FCSTD DOCUMENT  (FreeCAD 0.19R24267 (Git))
Label: single_dot_display_assem
License: All rights reserved
LicenseURL: http://en.wikipedia.org/wiki/All_rights_reserved
objects: App::Link×3, App::DocumentObjectGroup×2, PartDesign::CoordinateSystem×1, App::FeaturePython×1, App::Part×1
note: 1 computed .brp shape members not serialized (recipe doc carries the construction recipe); baked Part::Feature solids carry a one-line shape summary decoded from their .brp
EXTERNAL_REF file=single_dot_dislay_box.FCStd obj=Local_CS
EXTERNAL_REF file=single_dot_dislay_box.FCStd obj=Body
EXTERNAL_REF file=single_dot_display_lid.FCStd obj=Local_CS
EXTERNAL_REF file=single_dot_display_lid.FCStd obj=Body
EXTERNAL_REF file=mom_switch.FCStd obj=Local_CS
EXTERNAL_REF file=single_dot_display_lid.FCStd obj=Local_CS001
EXTERNAL_REF file=mom_switch.FCStd obj=Body

FEATURE [App::DocumentObjectGroup] Parts
FEATURE [PartDesign::CoordinateSystem] LCS_Origin
  AttacherType = Attacher::AttachEngine3D
  MapMode = 2
  Support = -> [X_Axis]
FEATURE [App::DocumentObjectGroup] Constraints
FEATURE [App::FeaturePython] Variables  # WARN: FeaturePython — macro-defined, semantics opaque (R4)
FEATURE [App::Link] single_dot_dislay_box_Body
  AssemblyType = Asm4EE
  AttachedBy = #Local_CS
  AttachedTo = Parent Assembly#LCS_Origin
  LinkPlacement = pos=(55,22.5,-45) rot=(0,0,-1;1.5708rad)
  LinkedObject = -> <external single_dot_dislay_box.FCStd>#Body
  Placement = pos=(55,22.5,-45) rot=(0,0,-1;1.5708rad)
  expr: Placement = LCS_Origin.Placement * AttachmentOffset * single_dot_dislay_box#Local_CS.Placement ^ -1
FEATURE [App::Link] single_dot_display_lid_Body
  AssemblyType = Asm4EE
  AttachedBy = #Local_CS
  AttachedTo = single_dot_dislay_box_Body#Local_CS
  LinkPlacement = pos=(87.5,22.5,0) rot=(0,0,1;1.5708rad)
  LinkedObject = -> <external single_dot_display_lid.FCStd>#Body
  Placement = pos=(87.5,22.5,0) rot=(0,0,1;1.5708rad)
  expr: Placement = single_dot_dislay_box_Body.Placement * single_dot_dislay_box#Local_CS.Placement * AttachmentOffset * single_dot_display_lid#Local_CS.Placement ^ -1
FEATURE [App::Link] Unnamed1_Body
  AssemblyType = Asm4EE
  AttachedBy = #Local_CS
  AttachedTo = single_dot_display_lid_Body#Local_CS001
  LinkPlacement = pos=(27.5,22.5,-32) rot=(0,0,1;4.71239rad)
  LinkedObject = -> <external mom_switch.FCStd>#Body
  Placement = pos=(27.5,22.5,-32) rot=(0,0,1;4.71239rad)
  expr: Placement = single_dot_display_lid_Body.Placement * single_dot_display_lid#Local_CS001.Placement * AttachmentOffset * mom_switch#Local_CS.Placement ^ -1
FEATURE [App::Part] Model
  Configuration = 0
  Group = -> [LCS_Origin,Constraints,Variables,single_dot_dislay_box_Body,single_dot_display_lid_Body,Unnamed1_Body]
  Origin = -> Origin
  Type = Assembly4 Model

RESOLVED EXTERNAL PARTS (link-assembly join: the EXTERNAL_REF files above that resolve inside this repo's crawl, each included once):
---- part mom_switch.FCStd = doc fcstd_50052116598c ----
FCSTD DOCUMENT  (FreeCAD 0.19R24267 (Git))
Label: mom_switch
License: All rights reserved
LicenseURL: http://en.wikipedia.org/wiki/All_rights_reserved
objects: Sketcher::SketchObject×5, PartDesign::Pad×4, PartDesign::Pocket×1, PartDesign::Mirrored×1, PartDesign::Chamfer×1, PartDesign::CoordinateSystem×1, PartDesign::Body×1
note: 20 computed .brp shape members not serialized (recipe doc carries the construction recipe); baked Part::Feature solids carry a one-line shape summary decoded from their .brp

FEATURE [Sketcher::SketchObject] Sketch
  FullyConstrained = true
  MapMode = 5
  Support = -> [XY_Plane]
  sketch-geometry (4):
    g0: LineSegment StartX=-16.5 StartY=9.5 StartZ=0 EndX=16.5 EndY=9.5 EndZ=0
    g1: LineSegment StartX=16.5 StartY=9.5 StartZ=0 EndX=16.5 EndY=-9.5 EndZ=0
    g2: LineSegment StartX=16.5 StartY=-9.5 StartZ=0 EndX=-16.5 EndY=-9.5 EndZ=0
    g3: LineSegment StartX=-16.5 StartY=-9.5 StartZ=0 EndX=-16.5 EndY=9.5 EndZ=0
  constraints (12):
    c: Coincident(g0,g1)
    c: Coincident(g1,g2)
    c: Coincident(g2,g3)
    c: Coincident(g3,g0)
    c: Horizontal(g0)
    c: Horizontal(g2)
    c: Vertical(g1)
    c: Vertical(g3)
    c: Distance(g0) = 33
    c: Distance(g3) = 19
    c: DistanceX(g0) = 16.5
    c: DistanceY(g0) = 9.5
FEATURE [PartDesign::Pad] Pad
  Direction = (1,1,1)
  Length = 25
  Length2 = 100
  Profile = -> Sketch
  Refine = true
  Type = 0
FEATURE [Sketcher::SketchObject] Sketch001
  FullyConstrained = true
  MapMode = 5
  Placement = pos=(0,0,25) rot=(0,0,1;0rad)
  Support = -> [Pad]
  sketch-geometry (1):
    g0: Circle CenterX=0 CenterY=0 CenterZ=0 NormalX=0 NormalY=0 NormalZ=1 AngleXU=0 Radius=6
  constraints (2):
    c: Coincident(g0,g-1)
    c: Radius(g0) = 6
FEATURE [PartDesign::Pad] Pad001
  BaseFeature = -> Pad
  Direction = (1,1,1)
  Length = 12
  Length2 = 100
  Profile = -> Sketch001
  Refine = true
  Type = 0
FEATURE [Sketcher::SketchObject] Sketch002
  FullyConstrained = true
  MapMode = 5
  Placement = pos=(0,0,37) rot=(0,0,1;0rad)
  Support = -> [Pad001]
  sketch-geometry (1):
    g0: Circle CenterX=0 CenterY=0 CenterZ=0 NormalX=0 NormalY=0 NormalZ=1 AngleXU=0 Radius=2
  constraints (2):
    c: Coincident(g0,g-1)
    c: Radius(g0) = 2
FEATURE [PartDesign::Pad] Pad002
  BaseFeature = -> Pad001
  Direction = (1,1,1)
  Length = 3.6
  Length2 = 100
  Profile = -> Sketch002
  Refine = true
  Type = 0
FEATURE [Sketcher::SketchObject] Sketch003
  FullyConstrained = true
  MapMode = 5
  Placement = pos=(0,0,40.6) rot=(0,0,1;0rad)
  Support = -> [Pad002]
  sketch-geometry (5):
    g0: LineSegment StartX=4.5 StartY=-4.5 StartZ=0 EndX=4.5 EndY=4.5 EndZ=0
    g1: LineSegment StartX=4.5 StartY=4.5 StartZ=0 EndX=-4.5 EndY=4.5 EndZ=0
    g2: LineSegment StartX=-4.5 StartY=4.5 StartZ=0 EndX=-4.5 EndY=-4.5 EndZ=0
    g3: LineSegment StartX=-4.5 StartY=-4.5 StartZ=0 EndX=4.5 EndY=-4.5 EndZ=0
    g4: Circle CenterX=0 CenterY=0 CenterZ=0 NormalX=0 NormalY=0 NormalZ=1 AngleXU=0 Radius=6.36396
  constraints (14):
    c: Coincident(g0,g1)
    c: Coincident(g1,g2)
    c: Coincident(g2,g3)
    c: Coincident(g3,g0)
    c: Equal(g0,g1)
    c: Equal(g0,g2)
    c: Equal(g0,g3)
    c: PointOnObject(g0,g4)
    c: PointOnObject(g1,g4)
    c: PointOnObject(g2,g4)
    c: PointOnObject(g3,g4)
    c: Coincident(g4,g-1)
    c: Horizontal(g1)
    c: Distance(g1) = 9
FEATURE [PartDesign::Pad] Pad003
  BaseFeature = -> Pad002
  Direction = (1,1,1)
  Length = 23
  Length2 = 100
  Profile = -> Sketch003
  Refine = true
  Type = 0
FEATURE [Sketcher::SketchObject] Sketch004
  ExternalGeometry = -> [Pad003]
  FullyConstrained = false
  MapMode = 5
  Placement = pos=(4e-16,-4.5,0) rot=(1,0,0;1.5708rad)
  Support = -> [Pad003]
  sketch-geometry (3):
    g0: LineSegment StartX=-4.5 StartY=40.6 StartZ=0 EndX=-2.21452 EndY=63.6 EndZ=0
    g1: LineSegment StartX=-2.21452 StartY=63.6 StartZ=0 EndX=-4.5 EndY=63.6 EndZ=0
    g2: LineSegment StartX=-4.5 StartY=40.6 StartZ=0 EndX=-4.5 EndY=63.6 EndZ=0
  constraints (6):
    c: Coincident(g0,g-4)
    c: PointOnObject(g0,g-5)
    c: Coincident(g1,g0)
    c: Coincident(g1,g-5)
    c: Coincident(g2,g0)
    c: Coincident(g2,g1)
FEATURE [PartDesign::Pocket] Pocket
  BaseFeature = -> Pad003
  Length = 13
  Length2 = 100
  Profile = -> Sketch004
  Refine = true
  Type = 0
FEATURE [PartDesign::Mirrored] Mirrored
  BaseFeature = -> Pocket
  MirrorPlane = -> Sketch004 [V_Axis]
  Originals = -> [Pocket]
  Refine = true
FEATURE [PartDesign::Chamfer] Chamfer
  Angle = 45
  Base = -> Mirrored [Edge10,Edge2,Edge6,Edge4,Edge11,Edge8,Edge3,Edge7,Edge9,Edge13,Edge12,Edge1]
  BaseFeature = -> Mirrored
  ChamferType = 0
  FlipDirection = false
  Refine = true
  Size = 1
  Size2 = 1
  SupportTransform = false
FEATURE [PartDesign::CoordinateSystem] Local_CS  label="switch_center"
  AttacherType = Attacher::AttachEngine3D
  MapMode = 5
  Placement = pos=(0,0,37) rot=(0,0,1;0rad)
  Support = -> [Chamfer]
FEATURE [PartDesign::Body] Body
  Group = -> [Sketch,Pad,Sketch001,Pad001,Sketch002,Pad002,Sketch003,Pad003,Sketch004,Pocket,Mirrored,Chamfer,Local_CS]
  Origin = -> Origin
  Tip = -> Chamfer
---- part single_dot_dislay_box.FCStd = doc fcstd_fc865e79ae6e ----
FCSTD DOCUMENT  (FreeCAD 0.19R24267 (Git))
Label: single_dot_dislay_box
License: All rights reserved
LicenseURL: http://en.wikipedia.org/wiki/All_rights_reserved
objects: Sketcher::SketchObject×5, PartDesign::Pad×3, PartDesign::Pocket×2, PartDesign::CoordinateSystem×1, PartDesign::Body×1
note: 17 computed .brp shape members not serialized (recipe doc carries the construction recipe); baked Part::Feature solids carry a one-line shape summary decoded from their .brp

FEATURE [Sketcher::SketchObject] Sketch
  FullyConstrained = true
  MapMode = 5
  Support = -> [XY_Plane]
  sketch-geometry (4):
    g0: LineSegment StartX=-30 StartY=62.5 StartZ=0 EndX=30 EndY=62.5 EndZ=0
    g1: LineSegment StartX=30 StartY=62.5 StartZ=0 EndX=30 EndY=-62.5 EndZ=0
    g2: LineSegment StartX=30 StartY=-62.5 StartZ=0 EndX=-30 EndY=-62.5 EndZ=0
    g3: LineSegment StartX=-30 StartY=-62.5 StartZ=0 EndX=-30 EndY=62.5 EndZ=0
  constraints (12):
    c: Coincident(g0,g1)
    c: Coincident(g1,g2)
    c: Coincident(g2,g3)
    c: Coincident(g3,g0)
    c: Horizontal(g0)
    c: Horizontal(g2)
    c: Vertical(g1)
    c: Vertical(g3)
    c: Distance(g0) = 60
    c: Distance(g3) = 125
    c: DistanceX(g-2,g0) = 30
    c: DistanceY(g-1,g0) = 62.5
FEATURE [PartDesign::Pad] Pad
  Direction = (1,1,1)
  Length = 45
  Length2 = 100
  Profile = -> Sketch
  Refine = true
  Type = 0
FEATURE [Sketcher::SketchObject] Sketch001
  ExternalGeometry = -> [Pad]
  FullyConstrained = true
  MapMode = 5
  Placement = pos=(0,0,45) rot=(0,0,1;0rad)
  Support = -> [Pad]
  sketch-geometry (4):
    g0: LineSegment StartX=-27 StartY=59.5 StartZ=0 EndX=27 EndY=59.5 EndZ=0
    g1: LineSegment StartX=27 StartY=59.5 StartZ=0 EndX=27 EndY=-59.5 EndZ=0
    g2: LineSegment StartX=27 StartY=-59.5 StartZ=0 EndX=-27 EndY=-59.5 EndZ=0
    g3: LineSegment StartX=-27 StartY=-59.5 StartZ=0 EndX=-27 EndY=59.5 EndZ=0
  constraints (12):
    c: Coincident(g0,g1)
    c: Coincident(g1,g2)
    c: Coincident(g2,g3)
    c: Coincident(g3,g0)
    c: Horizontal(g0)
    c: Horizontal(g2)
    c: Vertical(g1)
    c: Vertical(g3)
    c: DistanceX(g0,g-5) = -3
    c: DistanceY(g0,g-5) = 3
    c: DistanceX(g1,g-4) = 3
    c: DistanceY(g1,g-4) = -3
FEATURE [PartDesign::Pocket] Pocket
  BaseFeature = -> Pad
  Length = 42
  Length2 = 100
  Profile = -> Sketch001
  Refine = true
  Type = 0
FEATURE [Sketcher::SketchObject] Sketch002
  ExternalGeometry = -> [Pocket]
  FullyConstrained = false
  MapMode = 5
  Placement = pos=(0,0,45) rot=(0,0,1;0rad)
  Support = -> [Pocket]
  sketch-geometry (23):
    g0: LineSegment StartX=30 StartY=-62.5 StartZ=0 EndX=30 EndY=-55 EndZ=0
    g1: LineSegment StartX=30 StartY=-55 StartZ=0 EndX=22.5 EndY=-55 EndZ=0
    g2: Circle CenterX=22.5 CenterY=-55 CenterZ=0 NormalX=0 NormalY=0 NormalZ=1 AngleXU=0 Radius=2.25
    g3: ArcOfCircle CenterX=22.5 CenterY=-55 CenterZ=0 NormalX=0 NormalY=0 NormalZ=1 AngleXU=0 Radius=3.75 StartAngle=1.5708 EndAngle=3.14159
    g4: LineSegment StartX=18.75 StartY=-60.4455 StartZ=0 EndX=18.75 EndY=-55 EndZ=0
    g5: LineSegment StartX=27.7509 StartY=-51.25 StartZ=0 EndX=22.5 EndY=-51.25 EndZ=0
    g6: LineSegment StartX=27.7509 StartY=-51.25 StartZ=0 EndX=27 EndY=-59.5 EndZ=0
    g7: LineSegment StartX=18.75 StartY=-60.4455 StartZ=0 EndX=27 EndY=-59.5 EndZ=0
    g8: LineSegment StartX=-18.75 StartY=-60.4455 StartZ=0 EndX=-27 EndY=-59.5 EndZ=0
    g9: LineSegment StartX=-18.75 StartY=-60.4455 StartZ=0 EndX=-18.75 EndY=-55 EndZ=0
    g10: ArcOfCircle CenterX=-22.5 CenterY=-55 CenterZ=0 NormalX=0 NormalY=0 NormalZ=1 AngleXU=0 Radius=3.75 StartAngle=0 EndAngle=1.5708
    g11: LineSegment StartX=-27.7509 StartY=-51.25 StartZ=0 EndX=-22.5 EndY=-51.25 EndZ=0
    g12: LineSegment StartX=-27.7509 StartY=-51.25 StartZ=0 EndX=-27 EndY=-59.5 EndZ=0
    g13: LineSegment StartX=-18.75 StartY=60.4455 StartZ=0 EndX=-27 EndY=59.5 EndZ=0
    g14: LineSegment StartX=-27.7509 StartY=51.25 StartZ=0 EndX=-27 EndY=59.5 EndZ=0
    g15: LineSegment StartX=-27.7509 StartY=51.25 StartZ=0 EndX=-22.5 EndY=51.25 EndZ=0
    g16: ArcOfCircle CenterX=-22.5 CenterY=55 CenterZ=0 NormalX=0 NormalY=0 NormalZ=1 AngleXU=0 Radius=3.75 StartAngle=4.71239 EndAngle=6.28319
    g17: LineSegment StartX=-18.75 StartY=60.4455 StartZ=0 EndX=-18.75 EndY=55 EndZ=0
    g18: LineSegment StartX=18.75 StartY=60.4455 StartZ=0 EndX=18.75 EndY=55 EndZ=0
    g19: LineSegment StartX=18.75 StartY=60.4455 StartZ=0 EndX=27 EndY=59.5 EndZ=0
    g20: ArcOfCircle CenterX=22.5 CenterY=55 CenterZ=0 NormalX=0 NormalY=0 NormalZ=1 AngleXU=0 Radius=3.75 StartAngle=3.14159 EndAngle=4.71239
    g21: LineSegment StartX=27.7509 StartY=51.25 StartZ=0 EndX=22.5 EndY=51.25 EndZ=0
    g22: LineSegment StartX=27.7509 StartY=51.25 StartZ=0 EndX=27 EndY=59.5 EndZ=0
  constraints (42):
    c: Coincident(g0,g-4)
    c: PointOnObject(g0,g-4)
    c: Coincident(g1,g0)
    c: Horizontal(g1)
    c: Distance(g1) = 7.5
    c: Equal(g0,g1)
    c: Coincident(g2,g1)
    c: Radius(g2) = 2.25
    c: Coincident(g3,g1)
    c: Radius(g3) = 3.75
    c: Vertical(g4)
    c: Horizontal(g5)
    c: Tangent(g3,g4) = 1.5708
    c: Tangent(g3,g5) = -1.5708
    c: Coincident(g6,g5)
    c: Coincident(g6,g-6)
    c: Coincident(g7,g4)
    c: Coincident(g7,g6)
    c: Radius(g10) = 3.75
    c: Vertical(g9)
    c: Horizontal(g11)
    c: Tangent(g10,g9) = -1.5708
    c: Tangent(g10,g11) = 1.5708
    c: Coincident(g12,g11)
    c: Coincident(g8,g9)
    c: Coincident(g8,g12)
    c: Radius(g20) = 3.75
    c: Vertical(g18)
    c: Horizontal(g21)
    c: Tangent(g20,g18) = -1.5708
    c: Tangent(g20,g21) = 1.5708
    c: Coincident(g22,g21)
    c: Coincident(g19,g18)
    c: Coincident(g19,g22)
    c: Radius(g16) = 3.75
    c: Vertical(g17)
    c: Horizontal(g15)
    c: Tangent(g16,g17) = 1.5708
    c: Tangent(g16,g15) = -1.5708
    c: Coincident(g14,g15)
    c: Coincident(g13,g17)
    c: Coincident(g13,g14)
FEATURE [PartDesign::Pad] Pad001
  BaseFeature = -> Pocket
  Direction = (1,1,1)
  Length = 8
  Length2 = 100
  Profile = -> Sketch002
  Refine = true
  Reversed = true
  Type = 0
FEATURE [Sketcher::SketchObject] Sketch003
  ExternalGeometry = -> [Pad001]
  FullyConstrained = false
  MapMode = 5
  Placement = pos=(0,0,45) rot=(0,0,1;0rad)
  Support = -> [Pad001]
  sketch-geometry (4):
    g0: Circle CenterX=22.5 CenterY=55 CenterZ=0 NormalX=0 NormalY=0 NormalZ=1 AngleXU=0 Radius=2.25
    g1: Circle CenterX=-22.5 CenterY=55 CenterZ=0 NormalX=0 NormalY=0 NormalZ=1 AngleXU=0 Radius=2.25
    g2: Circle CenterX=22.5 CenterY=-55 CenterZ=0 NormalX=0 NormalY=0 NormalZ=1 AngleXU=0 Radius=2.25
    g3: Circle CenterX=-22.5 CenterY=-55 CenterZ=0 NormalX=0 NormalY=0 NormalZ=1 AngleXU=0 Radius=2.25
  constraints (5):
    c: Coincident(g0,g-3)
    c: Radius(g0) = 2.25
    c: Radius(g1) = 2.25
    c: Radius(g2) = 2.25
    c: Radius(g3) = 2.25
FEATURE [PartDesign::Pocket] Pocket001
  BaseFeature = -> Pad001
  Length = 7
  Length2 = 100
  Profile = -> Sketch003
  Refine = true
  Type = 0
FEATURE [PartDesign::CoordinateSystem] Local_CS  label="fastener"
  AttacherType = Attacher::AttachEngine3D
  MapMode = 11
  Placement = pos=(22.5,-55,45) rot=(0,0,1;1.5708rad)
  Support = -> [Pocket001]
FEATURE [Sketcher::SketchObject] Sketch004
  FullyConstrained = false
  MapMode = 5
  Placement = pos=(0,0,3) rot=(0,0,1;0rad)
  Support = -> [Pocket001]
  sketch-geometry (34):
    g0: LineSegment StartX=-20 StartY=8 StartZ=0 EndX=24 EndY=8 EndZ=0
    g1: LineSegment StartX=24 StartY=8 StartZ=0 EndX=24 EndY=-8 EndZ=0
    g2: LineSegment StartX=24 StartY=-8 StartZ=0 EndX=-20 EndY=-8 EndZ=0
    g3: LineSegment StartX=-20 StartY=-8 StartZ=0 EndX=-20 EndY=8 EndZ=0
    g4: LineSegment StartX=-18 StartY=8 StartZ=0 EndX=-18 EndY=10 EndZ=0
    g5: LineSegment StartX=-18 StartY=10 StartZ=0 EndX=-22 EndY=10 EndZ=0
    g6: LineSegment StartX=-22 StartY=10 StartZ=0 EndX=-22 EndY=6 EndZ=0
    g7: LineSegment StartX=-22 StartY=6 StartZ=0 EndX=-20 EndY=6 EndZ=0
    g8: Circle CenterX=-20 CenterY=8 CenterZ=0 NormalX=0 NormalY=0 NormalZ=1 AngleXU=0 Radius=2.82843
    g9: LineSegment StartX=-20 StartY=6 StartZ=0 EndX=-20 EndY=8 EndZ=0
    g10: LineSegment StartX=-18 StartY=8 StartZ=0 EndX=-20 EndY=8 EndZ=0
    g11: LineSegment StartX=-18 StartY=-8 StartZ=0 EndX=-18 EndY=-10 EndZ=0
    g12: LineSegment StartX=-18 StartY=-10 StartZ=0 EndX=-22 EndY=-10 EndZ=0
    g13: LineSegment StartX=-22 StartY=-10 StartZ=0 EndX=-22 EndY=-6 EndZ=0
    g14: LineSegment StartX=-22 StartY=-6 StartZ=0 EndX=-20 EndY=-6 EndZ=0
    g15: Circle CenterX=-20 CenterY=-8 CenterZ=0 NormalX=0 NormalY=0 NormalZ=1 AngleXU=0 Radius=2.82843
    g16: LineSegment StartX=-20 StartY=-6 StartZ=0 EndX=-20 EndY=-8 EndZ=0
    g17: LineSegment StartX=-18 StartY=-8 StartZ=0 EndX=-20 EndY=-8 EndZ=0
    g18: LineSegment StartX=0 StartY=0 StartZ=0 EndX=2 EndY=0 EndZ=0
    g19: LineSegment StartX=2 StartY=0 StartZ=0 EndX=2 EndY=-2.88853 EndZ=0
    g20: LineSegment StartX=22 StartY=8 StartZ=0 EndX=22 EndY=10 EndZ=0
    g21: LineSegment StartX=22 StartY=10 StartZ=0 EndX=26 EndY=10 EndZ=0
    g22: LineSegment StartX=26 StartY=10 StartZ=0 EndX=26 EndY=6 EndZ=0
    g23: LineSegment StartX=26 StartY=6 StartZ=0 EndX=24 EndY=6 EndZ=0
    g24: Circle CenterX=24 CenterY=8 CenterZ=0 NormalX=0 NormalY=0 NormalZ=1 AngleXU=0 Radius=2.82843
    g25: LineSegment StartX=24 StartY=6 StartZ=0 EndX=24 EndY=8 EndZ=0
    g26: LineSegment StartX=22 StartY=8 StartZ=0 EndX=24 EndY=8 EndZ=0
    g27: LineSegment StartX=22 StartY=-8 StartZ=0 EndX=22 EndY=-10 EndZ=0
    g28: LineSegment StartX=22 StartY=-10 StartZ=0 EndX=26 EndY=-10 EndZ=0
    g29: LineSegment StartX=26 StartY=-10 StartZ=0 EndX=26 EndY=-6 EndZ=0
    g30: LineSegment StartX=26 StartY=-6 StartZ=0 EndX=24 EndY=-6 EndZ=0
    g31: Circle CenterX=24 CenterY=-8 CenterZ=0 NormalX=0 NormalY=0 NormalZ=1 AngleXU=0 Radius=2.82843
    g32: LineSegment StartX=24 StartY=-6 StartZ=0 EndX=24 EndY=-8 EndZ=0
    g33: LineSegment StartX=22 StartY=-8 StartZ=0 EndX=24 EndY=-8 EndZ=0
  constraints (61):
    c: Coincident(g0,g1)
    c: Coincident(g1,g2)
    c: Coincident(g2,g3)
    c: Coincident(g3,g0)
    c: Horizontal(g0)
    c: Horizontal(g2)
    c: Vertical(g1)
    c: Vertical(g3)
    c: Distance(g0) = 44
    c: Distance(g3) = 16
    c: DistanceX(g0) = 24
    c: DistanceY(g0) = 8
    c: Coincident(g4,g5)
    c: Coincident(g5,g6)
    c: Coincident(g6,g7)
    c: PointOnObject(g4,g8)
    c: PointOnObject(g5,g8)
    c: PointOnObject(g6,g8)
    c: Coincident(g8,g0)
    c: Horizontal(g7)
    c: PointOnObject(g4,g0)
    c: PointOnObject(g7,g3)
    c: Coincident(g9,g7)
    c: Coincident(g9,g0)
    c: Coincident(g10,g4)
    c: Coincident(g10,g9)
    c: Coincident(g11,g12)
    c: Coincident(g12,g13)
    c: Coincident(g13,g14)
    c: PointOnObject(g11,g15)
    c: PointOnObject(g12,g15)
    c: PointOnObject(g13,g15)
    c: Horizontal(g14)
    c: Coincident(g16,g14)
    c: Coincident(g17,g11)
    c: Coincident(g17,g16)
    c: Coincident(g18,g-1)
    c: PointOnObject(g18,g-1)
    c: Distance(g18) = 2
    c: Coincident(g19,g18)
    c: Vertical(g19)
    c: Coincident(g20,g21)
    c: Coincident(g21,g22)
    c: Coincident(g22,g23)
    c: PointOnObject(g20,g24)
    c: PointOnObject(g21,g24)
    c: PointOnObject(g22,g24)
    c: Horizontal(g23)
    c: Coincident(g25,g23)
    c: Coincident(g26,g20)
    c: Coincident(g26,g25)
    c: Coincident(g27,g28)
    c: Coincident(g28,g29)
    c: Coincident(g29,g30)
    c: PointOnObject(g27,g31)
    c: PointOnObject(g28,g31)
    c: PointOnObject(g29,g31)
    c: Horizontal(g30)
    c: Coincident(g32,g30)
    c: Coincident(g33,g27)
    c: Coincident(g33,g32)
FEATURE [PartDesign::Pad] Pad002
  BaseFeature = -> Pocket001
  Direction = (1,1,1)
  Length = 11
  Length2 = 100
  Profile = -> Sketch004
  Refine = true
  Type = 0
FEATURE [PartDesign::Body] Body
  Group = -> [Sketch,Pad,Sketch001,Pocket,Sketch002,Pad001,Sketch003,Pocket001,Local_CS,Sketch004,Pad002]
  Origin = -> Origin
  Tip = -> Pad002
---- part single_dot_display_lid.FCStd = doc fcstd_47c3f7db298e ----
FCSTD DOCUMENT  (FreeCAD 0.19R24267 (Git))
Label: single_dot_display_lid
License: All rights reserved
LicenseURL: http://en.wikipedia.org/wiki/All_rights_reserved
objects: Sketcher::SketchObject×10, PartDesign::Pocket×7, PartDesign::Pad×3, PartDesign::Mirrored×2, PartDesign::Chamfer×2, PartDesign::Point×2, PartDesign::CoordinateSystem×2, PartDesign::Line×1, PartDesign::Body×1
note: 42 computed .brp shape members not serialized (recipe doc carries the construction recipe); baked Part::Feature solids carry a one-line shape summary decoded from their .brp

FEATURE [Sketcher::SketchObject] Sketch
  FullyConstrained = false
  MapMode = 5
  Support = -> [XY_Plane]
  sketch-geometry (7):
    g0: LineSegment StartX=0 StartY=0 StartZ=0 EndX=0 EndY=17.9605 EndZ=0
    g1: LineSegment StartX=0 StartY=0 StartZ=0 EndX=0 EndY=-17.9605 EndZ=0
    g2: LineSegment StartX=0 StartY=-17.9605 StartZ=0 EndX=17.9605 EndY=-1.3181e-12 EndZ=0
    g3: LineSegment StartX=17.9605 StartY=-1.3198e-12 StartZ=0 EndX=7.8018e-12 EndY=17.9605 EndZ=0
    g4: LineSegment StartX=7.8006e-12 StartY=17.9605 StartZ=0 EndX=-17.9605 EndY=5.5387e-12 EndZ=0
    g5: LineSegment StartX=-17.9605 StartY=5.5387e-12 StartZ=0 EndX=0 EndY=-17.9605 EndZ=0
    g6: Circle CenterX=0 CenterY=0 CenterZ=0 NormalX=0 NormalY=0 NormalZ=1 AngleXU=0 Radius=17.9605
  constraints (19):
    c: Coincident(g0,g-1)
    c: Vertical(g0)
    c: Vertical(g1)
    c: Coincident(g2,g3)
    c: Coincident(g3,g4)
    c: Coincident(g4,g5)
    c: Coincident(g5,g2)
    c: Equal(g2,g3)
    c: Equal(g2,g4)
    c: Equal(g2,g5)
    c: PointOnObject(g2,g6)
    c: PointOnObject(g3,g6)
    c: PointOnObject(g4,g6)
    c: PointOnObject(g5,g6)
    c: Coincident(g6,g-1)
    c: Coincident(g5,g1)
    c: Coincident(g1,g-1)
    c: Equal(g1,g0)
    c: Distance(g4) = 25.4
FEATURE [PartDesign::Pad] Pad
  AllowMultiFace = false
  Direction = (1,1,1)
  Length = 22
  Length2 = 100
  Profile = -> Sketch
  Type = 0
FEATURE [Sketcher::SketchObject] Sketch001
  FullyConstrained = false
  MapMode = 5
  Placement = pos=(0,0,22) rot=(0,0,1;0rad)
  Support = -> [Pad]
  sketch-geometry (6):
    g0: LineSegment StartX=0 StartY=14.8492 StartZ=0 EndX=-14.8492 EndY=-1.8e-15 EndZ=0
    g1: LineSegment StartX=-14.8492 StartY=-1.8e-15 StartZ=0 EndX=0 EndY=-14.8492 EndZ=0
    g2: LineSegment StartX=8e-16 StartY=-14.8492 StartZ=0 EndX=14.8492 EndY=0 EndZ=0
    g3: LineSegment StartX=14.8492 StartY=0 StartZ=0 EndX=0 EndY=14.8492 EndZ=0
    g4: Circle CenterX=0 CenterY=0 CenterZ=0 NormalX=0 NormalY=0 NormalZ=1 AngleXU=0 Radius=14.8492
    g5: LineSegment StartX=0 StartY=0 StartZ=0 EndX=0 EndY=14.8492 EndZ=0
  constraints (16):
    c: Coincident(g0,g1)
    c: Coincident(g1,g2)
    c: Coincident(g2,g3)
    c: Coincident(g3,g0)
    c: Equal(g0,g1)
    c: Equal(g0,g2)
    c: Equal(g0,g3)
    c: PointOnObject(g0,g4)
    c: PointOnObject(g1,g4)
    c: PointOnObject(g2,g4)
    c: PointOnObject(g3,g4)
    c: Coincident(g4,g-1)
    c: PointOnObject(g3,g-2)
    c: Coincident(g5,g-1)
    c: Coincident(g0,g5)
    c: Distance(g0) = 21
FEATURE [PartDesign::Pocket] Pocket
  AllowMultiFace = false
  BaseFeature = -> Pad
  Length = 20
  Length2 = 100
  Profile = -> Sketch001
  Type = 0
FEATURE [Sketcher::SketchObject] Sketch002
  ExternalGeometry = -> [Pocket]
  FullyConstrained = false
  MapMode = 5
  Placement = pos=(0,0,22) rot=(0,0,1;0rad)
  Support = -> [Pocket]
  sketch-geometry (7):
    g0: LineSegment StartX=-8e-16 StartY=17.9605 StartZ=0 EndX=0 EndY=14.8492 EndZ=0
    g1: LineSegment StartX=-3.11127 StartY=14.8492 StartZ=0 EndX=-17.9605 EndY=3.6e-15 EndZ=0
    g2: LineSegment StartX=-17.9605 StartY=3.6e-15 StartZ=0 EndX=-3.11127 EndY=-14.8492 EndZ=0
    g3: LineSegment StartX=-14.8492 StartY=9e-16 StartZ=0 EndX=0 EndY=-14.8492 EndZ=0
    g4: LineSegment StartX=-14.8492 StartY=9e-16 StartZ=0 EndX=0 EndY=14.8492 EndZ=0
    g5: LineSegment StartX=0 StartY=14.8492 StartZ=0 EndX=-3.11127 EndY=14.8492 EndZ=0
    g6: LineSegment StartX=0 StartY=-14.8492 StartZ=0 EndX=-3.11127 EndY=-14.8492 EndZ=0
  constraints (16):
    c: Coincident(g0,g-4)
    c: Coincident(g1,g-4)
    c: Coincident(g2,g1)
    c: Coincident(g3,g-5)
    c: Coincident(g4,g3)
    c: Coincident(g4,g0)
    c: Coincident(g5,g4)
    c: Horizontal(g5)
    c: Coincident(g1,g5)
    c: Coincident(g6,g3)
    c: Horizontal(g6)
    c: Coincident(g2,g6)
    c: PointOnObject(g1,g-4)
    c: Coincident(g4,g-6)
    c: PointOnObject(g2,g-7)
    c: Coincident(g3,g-9)
FEATURE [PartDesign::Pocket] Pocket001
  AllowMultiFace = false
  BaseFeature = -> Pocket
  Length = 10
  Length2 = 100
  Profile = -> Sketch002
  Type = 0
FEATURE [PartDesign::Mirrored] Mirrored
  BaseFeature = -> Pocket001
  MirrorPlane = -> YZ_Plane
  Originals = -> [Pocket001]
FEATURE [Sketcher::SketchObject] Sketch003
  FullyConstrained = false
  MapMode = 5
  Placement = pos=(0,0,0) rot=(1,0,0;1.5708rad)
  Support = -> [XZ_Plane]
  sketch-geometry (1):
    g0: Circle CenterX=0 CenterY=19.6223 CenterZ=0 NormalX=0 NormalY=0 NormalZ=1 AngleXU=0 Radius=1
  constraints (2):
    c: PointOnObject(g0,g-2)
    c: Radius(g0) = 1
FEATURE [PartDesign::Pocket] Pocket002
  AllowMultiFace = false
  BaseFeature = -> Mirrored
  Length = 16.25
  Length2 = 16.25
  Profile = -> Sketch003
  Type = 4
FEATURE [Sketcher::SketchObject] Sketch004
  ExternalGeometry = -> [Pocket002]
  FullyConstrained = true
  MapMode = 5
  Placement = pos=(0,0,12) rot=(0,0,1;0rad)
  Support = -> [Pocket002]
  sketch-geometry (3):
    g0: LineSegment StartX=0 StartY=0 StartZ=0 EndX=8.98026 EndY=8.98026 EndZ=0
    g1: Circle CenterX=8.20244 CenterY=8.20244 CenterZ=0 NormalX=0 NormalY=0 NormalZ=1 AngleXU=0 Radius=1.1
    g2: GeomPoint X=7.42462 Y=7.42462 Z=0
  constraints (8):
    c: Coincident(g0,g-1)
    c: Angle(g-1,g0) = 0.785398
    c: PointOnObject(g1,g0)
    c: Tangent(g1,g-3)
    c: PointOnObject(g2,g0)
    c: PointOnObject(g2,g-4)
    c: PointOnObject(g2,g1)
    c: PointOnObject(g0,g-3)
FEATURE [PartDesign::Pad] Pad001
  AllowMultiFace = false
  BaseFeature = -> Pocket002
  Direction = (1,1,1)
  Length = 9
  Length2 = 100
  Profile = -> Sketch004
  Type = 0
FEATURE [PartDesign::Mirrored] Mirrored001
  BaseFeature = -> Pad001
  MirrorPlane = -> YZ_Plane
  Originals = -> [Pad001]
FEATURE [Sketcher::SketchObject] Sketch005
  FullyConstrained = false
  MapMode = 5
  Placement = pos=(0,0,2) rot=(0,0,1;0rad)
  Support = -> [Mirrored001]
  sketch-geometry (3):
    g0: Circle CenterX=-11 CenterY=0 CenterZ=0 NormalX=0 NormalY=0 NormalZ=1 AngleXU=0 Radius=1
    g1: LineSegment StartX=-11 StartY=0 StartZ=0 EndX=0 EndY=0 EndZ=0
    g2: Circle CenterX=11 CenterY=0 CenterZ=0 NormalX=0 NormalY=0 NormalZ=1 AngleXU=0 Radius=1
  constraints (6):
    c: PointOnObject(g0,g-1)
    c: Radius(g0) = 1
    c: Coincident(g1,g0)
    c: Coincident(g1,g-1)
    c: Distance(g1) = 11
    c: Radius(g2) = 1
FEATURE [PartDesign::Pocket] Pocket003
  AllowMultiFace = false
  BaseFeature = -> Mirrored001
  Length = 5
  Length2 = 100
  Profile = -> Sketch005
  Type = 0
FEATURE [Sketcher::SketchObject] Sketch006
  ExternalGeometry = -> [Pocket003]
  FullyConstrained = false
  MapMode = 5
  Placement = pos=(0,0,0) rot=(1,0,0;3.14159rad)
  Support = -> [Pocket003]
  sketch-geometry (10):
    g0: LineSegment StartX=-30 StartY=30 StartZ=0 EndX=30 EndY=30 EndZ=0
    g1: LineSegment StartX=30 StartY=30 StartZ=0 EndX=30 EndY=-95 EndZ=0
    g2: LineSegment StartX=30 StartY=-95 StartZ=0 EndX=-30 EndY=-95 EndZ=0
    g3: LineSegment StartX=-30 StartY=-95 StartZ=0 EndX=-30 EndY=30 EndZ=0
    g4: Circle CenterX=0 CenterY=-57.2874 CenterZ=0 NormalX=0 NormalY=0 NormalZ=1 AngleXU=0 Radius=6
    g5: LineSegment StartX=-3.59996e-11 StartY=17.5265 StartZ=0 EndX=-17.5265 EndY=-4.8956e-12 EndZ=0
    g6: LineSegment StartX=-17.5265 StartY=-4.8956e-12 StartZ=0 EndX=-3.67422e-11 EndY=-17.5265 EndZ=0
    g7: LineSegment StartX=-3.67433e-11 StartY=-17.5265 StartZ=0 EndX=17.5265 EndY=-5.6382e-12 EndZ=0
    g8: LineSegment StartX=17.5265 StartY=-5.6376e-12 StartZ=0 EndX=-3.59996e-11 EndY=17.5265 EndZ=0
    g9: Circle CenterX=-3.63706e-11 CenterY=-5.2673e-12 CenterZ=0 NormalX=0 NormalY=0 NormalZ=1 AngleXU=0 Radius=17.5265
  constraints (25):
    c: Coincident(g0,g1)
    c: Coincident(g1,g2)
    c: Coincident(g2,g3)
    c: Coincident(g3,g0)
    c: Horizontal(g0)
    c: Horizontal(g2)
    c: Vertical(g1)
    c: Vertical(g3)
    c: Distance(g0) = 60
    c: DistanceX(g-1,g0) = 30
    c: DistanceY(g-1,g0) = 30
    c: DistanceY(g1,g1) = 125
    c: PointOnObject(g4,g-2)
    c: Radius(g4) = 6
    c: Coincident(g5,g6)
    c: Coincident(g6,g7)
    c: Coincident(g7,g8)
    c: Coincident(g8,g5)
    c: Equal(g5,g6)
    c: Equal(g5,g7)
    c: Equal(g5,g8)
    c: PointOnObject(g5,g9)
    c: PointOnObject(g6,g9)
    c: PointOnObject(g7,g9)
    c: PointOnObject(g8,g9)
FEATURE [PartDesign::Pad] Pad002
  BaseFeature = -> Pocket003
  Direction = (1,1,1)
  Length = 5
  Length2 = 100
  Profile = -> Sketch006
  Refine = true
  Reversed = true
  Type = 0
FEATURE [PartDesign::Chamfer] Chamfer
  Angle = 45
  Base = -> Pad002 [Edge35,Edge37,Edge32,Edge29]
  BaseFeature = -> Pad002
  ChamferType = 0
  FlipDirection = false
  Refine = true
  Size = 3
  Size2 = 1
  SupportTransform = false
FEATURE [PartDesign::Chamfer] Chamfer001
  Angle = 45
  Base = -> Chamfer [Edge31,Edge36,Edge41,Edge35]
  BaseFeature = -> Chamfer
  ChamferType = 0
  FlipDirection = false
  Refine = true
  Size = 1
  Size2 = 1
  SupportTransform = false
FEATURE [Sketcher::SketchObject] Sketch007
  FullyConstrained = true
  MapMode = 5
  Placement = pos=(0,0,5) rot=(0,0,1;0rad)
  Support = -> [Chamfer001]
  sketch-geometry (2):
    g0: LineSegment StartX=0 StartY=0 StartZ=0 EndX=0 EndY=60 EndZ=0
    g1: Circle CenterX=0 CenterY=60 CenterZ=0 NormalX=0 NormalY=0 NormalZ=1 AngleXU=0 Radius=6
  constraints (5):
    c: Coincident(g0,g-1)
    c: PointOnObject(g0,g-2)
    c: Distance(g0) = 60
    c: Coincident(g1,g0)
    c: Radius(g1) = 6
FEATURE [PartDesign::Pocket] Pocket004
  BaseFeature = -> Chamfer001
  Length = 5
  Length2 = 100
  Profile = -> Sketch007
  Refine = true
  Type = 0
FEATURE [Sketcher::SketchObject] Sketch008
  ExternalGeometry = -> [Pocket004]
  FullyConstrained = false
  MapMode = 5
  Placement = pos=(0,0,5) rot=(0,0,1;0rad)
  Support = -> [Pocket004]
  sketch-geometry (11):
    g0: LineSegment StartX=-22.5 StartY=-22.5 StartZ=0 EndX=-22.5 EndY=87.5 EndZ=0
    g1: Circle CenterX=-22.5 CenterY=87.5 CenterZ=0 NormalX=0 NormalY=0 NormalZ=1 AngleXU=0 Radius=1.5
    g2: Circle CenterX=-22.5 CenterY=87.5 CenterZ=0 NormalX=0 NormalY=0 NormalZ=1 AngleXU=0 Radius=3
    g3: LineSegment StartX=-22.5 StartY=87.5 StartZ=0 EndX=-22.5 EndY=92 EndZ=0
    g4: LineSegment StartX=-22.5 StartY=87.5 StartZ=0 EndX=-27 EndY=87.5 EndZ=0
    g5: LineSegment StartX=-22.5 StartY=-22.5 StartZ=0 EndX=-22.5 EndY=32.5 EndZ=0
    g6: LineSegment StartX=-22.5 StartY=32.5 StartZ=0 EndX=12.6721 EndY=32.5 EndZ=0
    g7: LineSegment StartX=0 StartY=32.5 StartZ=0 EndX=0 EndY=49.2466 EndZ=0
    g8: Circle CenterX=22.5 CenterY=87.5 CenterZ=0 NormalX=0 NormalY=0 NormalZ=1 AngleXU=0 Radius=1.5
    g9: Circle CenterX=22.5 CenterY=-22.5 CenterZ=0 NormalX=0 NormalY=0 NormalZ=1 AngleXU=0 Radius=1.5
    g10: Circle CenterX=-22.5 CenterY=-22.5 CenterZ=0 NormalX=0 NormalY=0 NormalZ=1 AngleXU=0 Radius=1.5
  constraints (25):
    c: Vertical(g0)
    c: Radius(g1) = 1.5
    c: Coincident(g2,g1)
    c: Radius(g2) = 3
    c: Coincident(g3,g1)
    c: PointOnObject(g3,g-3)
    c: Vertical(g3)
    c: Coincident(g4,g1)
    c: PointOnObject(g4,g-5)
    c: Horizontal(g4)
    c: Equal(g4,g3)
    c: Distance(g3) = 4.5
    c: DistanceY(g-5,g0) = 4.5
    c: Coincident(g5,g0)
    c: Distance(g5) = 55
    c: PointOnObject(g5,g0)
    c: Coincident(g0,g1)
    c: Coincident(g6,g5)
    c: Horizontal(g6)
    c: PointOnObject(g7,g6)
    c: Vertical(g7)
    c: PointOnObject(g7,g-2)
    c: Radius(g8) = 1.5
    c: Radius(g10) = 1.5
    c: Radius(g9) = 1.5
FEATURE [PartDesign::Pocket] Pocket005
  BaseFeature = -> Pocket004
  Length = 5
  Length2 = 100
  Profile = -> Sketch008
  Refine = true
  Type = 0
FEATURE [Sketcher::SketchObject] Sketch009
  ExternalGeometry = -> [Pocket005]
  FullyConstrained = false
  MapMode = 5
  Placement = pos=(0,0,5) rot=(0,0,1;0rad)
  Support = -> [Pocket005]
  sketch-geometry (6):
    g0: Circle CenterX=-22.5 CenterY=87.5 CenterZ=0 NormalX=0 NormalY=0 NormalZ=1 AngleXU=0 Radius=3
    g1: Circle CenterX=22.5 CenterY=87.5 CenterZ=0 NormalX=0 NormalY=0 NormalZ=1 AngleXU=0 Radius=3
    g2: LineSegment StartX=-22.5 StartY=87.5 StartZ=0 EndX=-22.5 EndY=32.5 EndZ=0
    g3: LineSegment StartX=-22.5 StartY=32.5 StartZ=0 EndX=-8.09534 EndY=32.5 EndZ=0
    g4: Circle CenterX=-22.5 CenterY=-22.5 CenterZ=0 NormalX=0 NormalY=0 NormalZ=1 AngleXU=0 Radius=3
    g5: Circle CenterX=22.5 CenterY=-22.5 CenterZ=0 NormalX=0 NormalY=0 NormalZ=1 AngleXU=0 Radius=3
  constraints (10):
    c: Coincident(g0,g-4)
    c: Radius(g0) = 3
    c: Radius(g1) = 3
    c: Coincident(g2,g0)
    c: Vertical(g2)
    c: Distance(g2) = 55
    c: Coincident(g3,g2)
    c: Horizontal(g3)
    c: Radius(g4) = 3
    c: Radius(g5) = 3
FEATURE [PartDesign::Pocket] Pocket006
  BaseFeature = -> Pocket005
  Length = 1.6
  Length2 = 100
  Profile = -> Sketch009
  Refine = true
  Type = 0
FEATURE [PartDesign::Line] DatumLine
  AttacherType = Attacher::AttachEngineLine
  Length = 20
  MapMode = 19
  Placement = pos=(22.5,87.5,0) rot=(0,0,1;0rad)
  ResizeMode = 0
  Support = -> [Pocket006]
FEATURE [PartDesign::Point] DatumPoint
  AttacherType = Attacher::AttachEnginePoint
FEATURE [PartDesign::Point] DatumPoint001
  AttacherType = Attacher::AttachEnginePoint
  MapMode = 41
  Placement = pos=(22.5,87.5,0) rot=(0,0,1;0rad)
  Support = -> [Pocket006,DatumLine]
FEATURE [PartDesign::CoordinateSystem] Local_CS  label="fastener"
  AttacherType = Attacher::AttachEngine3D
  AttachmentOffset = pos=(0,0,0) rot=(0,0,-1;3.14159rad)
  MapMode = 11
  Placement = pos=(-22.5,87.5,0) rot=(0,0,-1;1.5708rad)
  Support = -> [Pocket006]
FEATURE [PartDesign::CoordinateSystem] Local_CS001  label="switch_center"
  AttacherType = Attacher::AttachEngine3D
  AttachmentOffset = pos=(0,0,0) rot=(0,0,1;1.5708rad)
  MapMode = 11
  Placement = pos=(0,60,5) rot=(0,0,1;3.14159rad)
  Support = -> [Pocket006]
FEATURE [PartDesign::Body] Body
  Group = -> [Sketch,Pad,Sketch001,Pocket,Sketch002,Pocket001,Mirrored,Sketch003,Pocket002,Sketch004,Pad001,Mirrored001,Sketch005,Pocket003,Sketch006,Pad002,Chamfer,Chamfer001,Sketch007,Pocket004,Sketch008,Pocket005,Sketch009,Pocket006,DatumLine,DatumPoint,DatumPoint001,Local_CS,Local_CS001]
  Origin = -> Origin
  Tip = -> Pocket006
